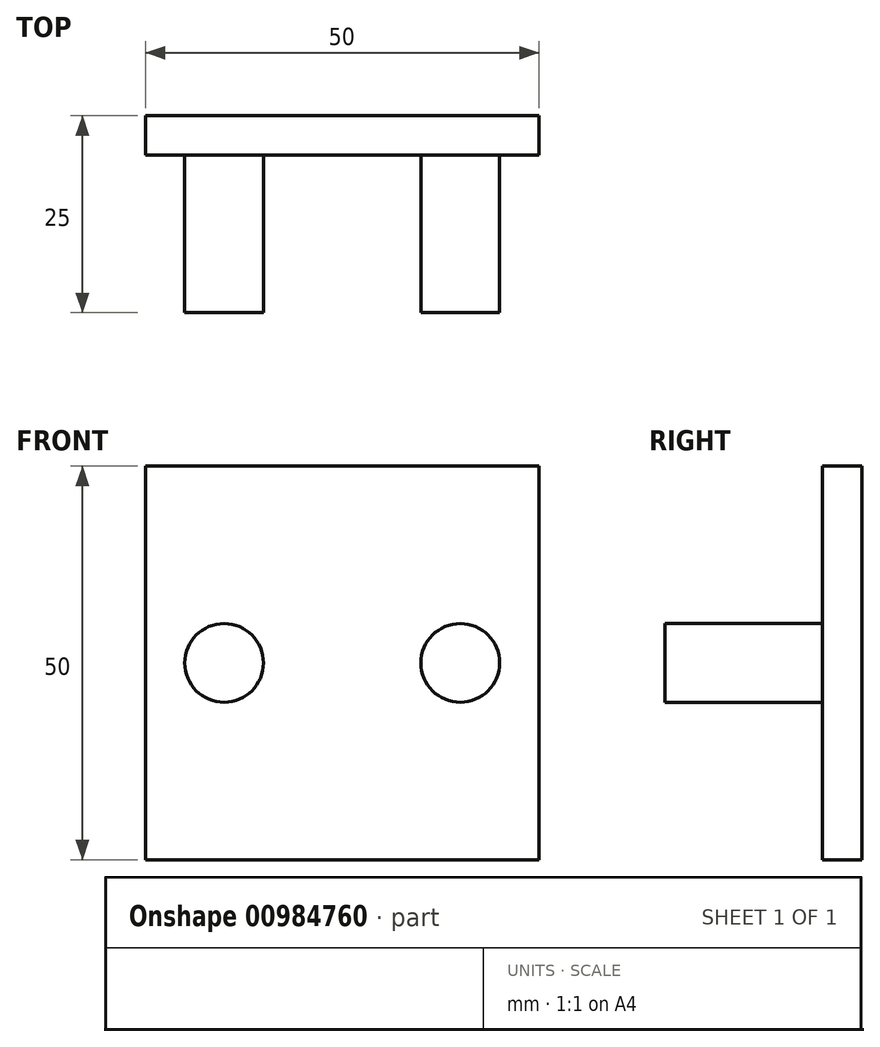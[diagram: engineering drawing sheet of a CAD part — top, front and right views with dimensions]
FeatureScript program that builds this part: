
annotation { "Feature Type Name" : "Feature", "Feature Type Description" : "" }
export const myFeature = defineFeature(function(context is Context, id is Id, definition is map)
    precondition{}
    {
        {
            var Q0;
            Q0=qCreatedBy(makeId("Front.planeOp"),FACE);
            var sketch = newSketch(context, id + "F0", { "sketchPlane" : qUnion([Q0])});
            skLineSegment(sketch, "E0.bottom", {"start": v(-25, 25) * mm, "end": v(25, 25) * mm});
            skLineSegment(sketch, "E0.top", {"start": v(-25, -25) * mm, "end": v(25, -25) * mm});
            skLineSegment(sketch, "E0.left", {"start": v(-25, 25) * mm, "end": v(-25, -25) * mm});
            skLineSegment(sketch, "E0.right", {"start": v(25, 25) * mm, "end": v(25, -25) * mm});
            skLineSegment(sketch, "E1", {"start": v(0, 25) * mm, "end": v(0, -25) * mm, "construction": true});
            skLineSegment(sketch, "E2", {"start": v(-25, 0) * mm, "end": v(25, 0) * mm, "construction": true});
            skSolve(sketch);
        }
        {
            var Q0;
            Q0=makeQuery(id+"F0.imprint","IMPRINT",FACE,{"disambiguationData":[TD([[makeQuery(id+"F0.imprint","IMPRINT",EDGE,{"derivedFrom":sQuery(id+"F0.wireOp",EDGE,"E0.bottom")}),-1.0]])]});
            extrude(context, id + "F1", {"entities" : qUnion([Q0]), "depth" : 5 * mm, "offsetDistance" : 25 * mm});
        }
        {
            var Q0;
            Q0=makeQuery(id+"F1.opExtrude","CAP_FACE",FACE,{"disambiguationData":[OSD([sQuery(id+"F0.wireOp",EDGE,"E0.bottom"),sQuery(id+"F0.wireOp",EDGE,"E0.top"),sQuery(id+"F0.wireOp",EDGE,"E0.left"),sQuery(id+"F0.wireOp",EDGE,"E0.right")])],"isStart":false});
            var sketch = newSketch(context, id + "F2", { "sketchPlane" : qUnion([Q0])});
            skCircle(sketch, "E3", {"center": v(-15, 0) * mm, "radius": 5 * mm});
            skCircle(sketch, "E4", {"center": v(15, 0) * mm, "radius": 5 * mm});
            skLineSegment(sketch, "E5", {"start": v(-15, 0) * mm, "end": v(15, 0) * mm, "construction": true});
            skSolve(sketch);
        }
        {
            var Q0;
            Q0 = qSketchRegion(id + "F2", true);
            extrude(context, id + "F3", {"entities" : qUnion([Q0]), "operationType" : NewBodyOperationType.ADD, "depth" : 20 * mm, "offsetDistance" : 25 * mm});
        }
    });
